# Revit family: LHF
name_source: partatom
category: Lighting Fixtures
revit_build: Autodesk Revit 2014 (Build: 20130308_1515(x64)
units: mm (PartAtom-declared; Revit-internal decimal feet)

## types (3) — shared parameters
Apparent Load = 0 VA
Assembly Code = D5020210
Backbox = Paint - Hubbell - Matte White
Color Filter = 16777215
Default Elevation = 48 "
Description = Litewave™ LHF Recessed Troffer
Diffuser = Soft Glow Lens, Blade Baffle, Perforated Blade
Dimming Lamp Color Temperature Shift = <None>
Distribution = Direct
Emit Shape Visible in Rendering = No
Glass = Glass - Hubbell - White
Lamp = Fluorescent
Load Classification = Lighting
Manufacturer = Litecontrol Lighting
Model = LHF
Mounting = Grid Ceiling, Narrow Face, Screw Slot
Power Factor = 0.9
Product Documentation Link = https://hubbellcdn.com
Product Page URL = https://www.hubbell.com
Tilt Angle = -90.00°
Type Comments = Lighting Fixtures
URL = https://www.hubbell.com
Voltage = 120 V
Warranty = 1 year warranty

## per-type parameters (varying)
| type | Emit from Rectangle Length | Emit from Rectangle Width | Photometric Web File | zz Length 1 | zz Length 2 |
| LHF-2x2 | 23 " | 23 " | LHF-G-D-22-2T5.ies | 24 " | 24 " |
| LHF-1x4 | 47 " | 11 " | LHF-G-D-22-2T5.ies | 48 " | 12 " |
| LHF-2x4 | 47 " | 23 " | LHF-G-D-24-2T5.ies | 48 " | 24 " |

## geometry (parser evidence)
native form markers: Sweep x2
no freeform markers — native parametric forms only
